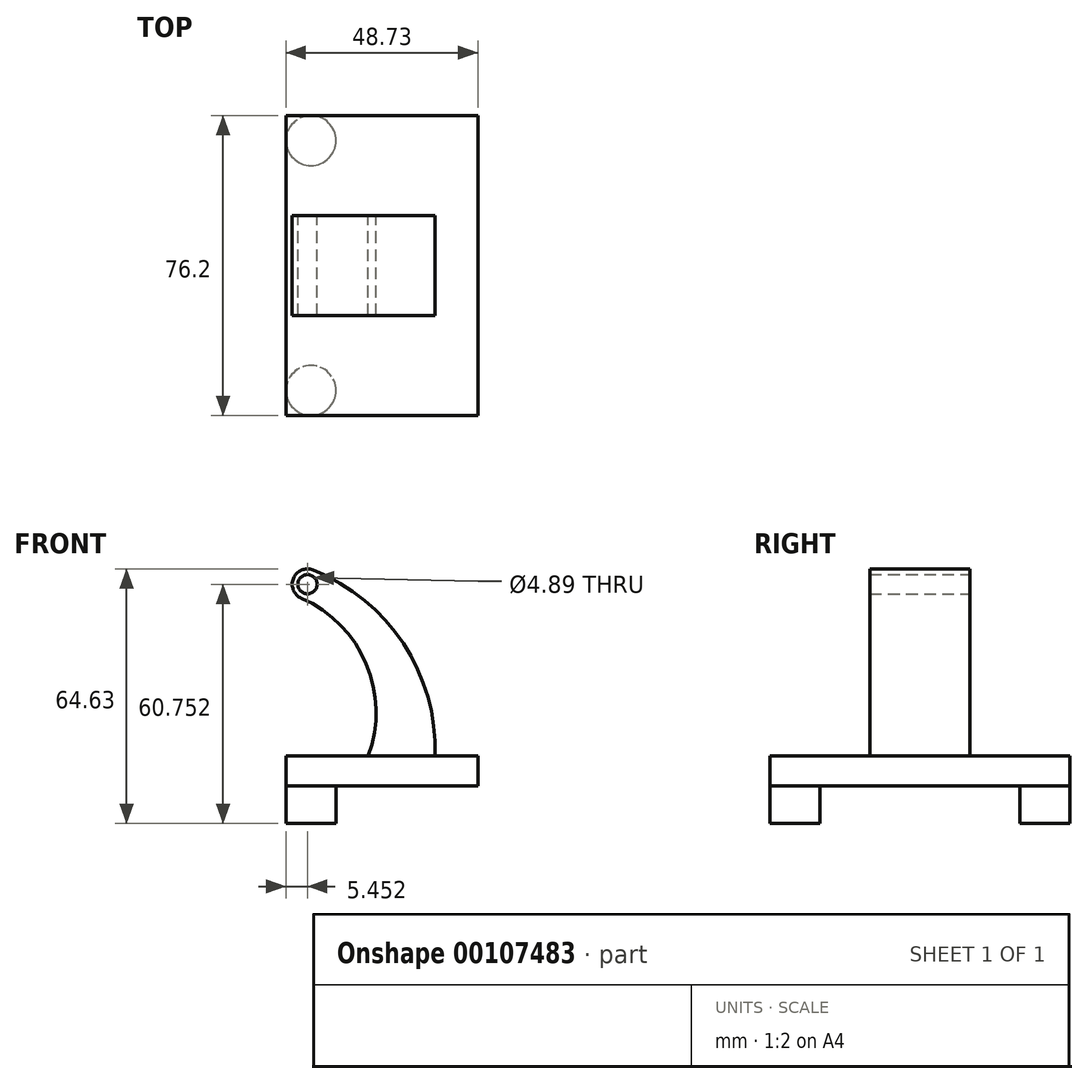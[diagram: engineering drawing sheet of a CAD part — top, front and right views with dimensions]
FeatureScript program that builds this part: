
annotation { "Feature Type Name" : "Feature", "Feature Type Description" : "" }
export const myFeature = defineFeature(function(context is Context, id is Id, definition is map)
    precondition{}
    {
        {
            var Q0;
            Q0=qCreatedBy(makeId("Front.planeOp"),FACE);
            var sketch = newSketch(context, id + "F0", { "sketchPlane" : qUnion([Q0])});
            skLineSegment(sketch, "E0", {"start": v(0, 0) * mm, "end": v(48.73, 0) * mm});
            skLineSegment(sketch, "E1", {"start": v(48.73, 0) * mm, "end": v(48.73, 7.56) * mm});
            skLineSegment(sketch, "E2", {"start": v(48.73, 7.56) * mm, "end": v(0, 7.56) * mm});
            skLineSegment(sketch, "E3", {"start": v(0, 7.56) * mm, "end": v(0, 0) * mm});
            skArc(sketch, "E4", {"start": v(37.85, 7.56) * mm, "mid": v(29.87, 36.11) * mm, "end": v(6.87, 54.83) * mm});
            skArc(sketch, "E5", {"start": v(20.86, 7.56) * mm, "mid": v(20.4, 31) * mm, "end": v(3.9, 47.67) * mm});
            skArc(sketch, "E6", {"start": v(6.87, 54.83) * mm, "mid": v(1.87, 52.7) * mm, "end": v(3.9, 47.67) * mm});
            skCircle(sketch, "E7", {"center": v(5.45, 51.22) * mm, "radius": 2.45 * mm});
            skSolve(sketch);
        }
        {
            var Q0;
            Q0=makeQuery(id+"F0.imprint","IMPRINT",FACE,{"disambiguationData":[TD([[makeQuery(id+"F0.imprint","IMPRINT",EDGE,{"derivedFrom":sQuery(id+"F0.wireOp",EDGE,"E0")}),1.0]])]});
            extrude(context, id + "F1", {"entities" : qUnion([Q0]), "endBound" : BoundingType.SYMMETRIC, "depth" : 76.2 * mm});
        }
        {
            var Q0;
            {var subQ1=sQuery(id+"F0.wireOp",EDGE,"E4");Q0=makeQuery(id+"F0.imprint","IMPRINT",FACE,{"disambiguationData":[TD([[makeQuery(id+"F0.imprint","IMPRINT",EDGE,{"derivedFrom":subQ1}),1.0]])]});}
            extrude(context, id + "F2", {"entities" : qUnion([Q0]), "operationType" : NewBodyOperationType.ADD, "endBound" : BoundingType.SYMMETRIC, "depth" : 25.4 * mm});
        }
        {
            var Q0;
            Q0=makeQuery(id+"F1.opExtrude","SWEPT_FACE",FACE,{"disambiguationData":[OSD([sQuery(id+"F0.wireOp",EDGE,"E0")])]});
            var sketch = newSketch(context, id + "F3", { "sketchPlane" : qUnion([Q0])});
            skCircle(sketch, "E8", {"center": v(6.35, -31.75) * mm, "radius": 6.35 * mm});
            skCircle(sketch, "E9", {"center": v(6.35, 31.75) * mm, "radius": 6.35 * mm});
            skSolve(sketch);
        }
        {
            var Q0;
            Q0 = qSketchRegion(id + "F3", true);
            extrude(context, id + "F4", {"entities" : qUnion([Q0]), "operationType" : NewBodyOperationType.ADD, "depth" : 9.52 * mm});
        }
    });
